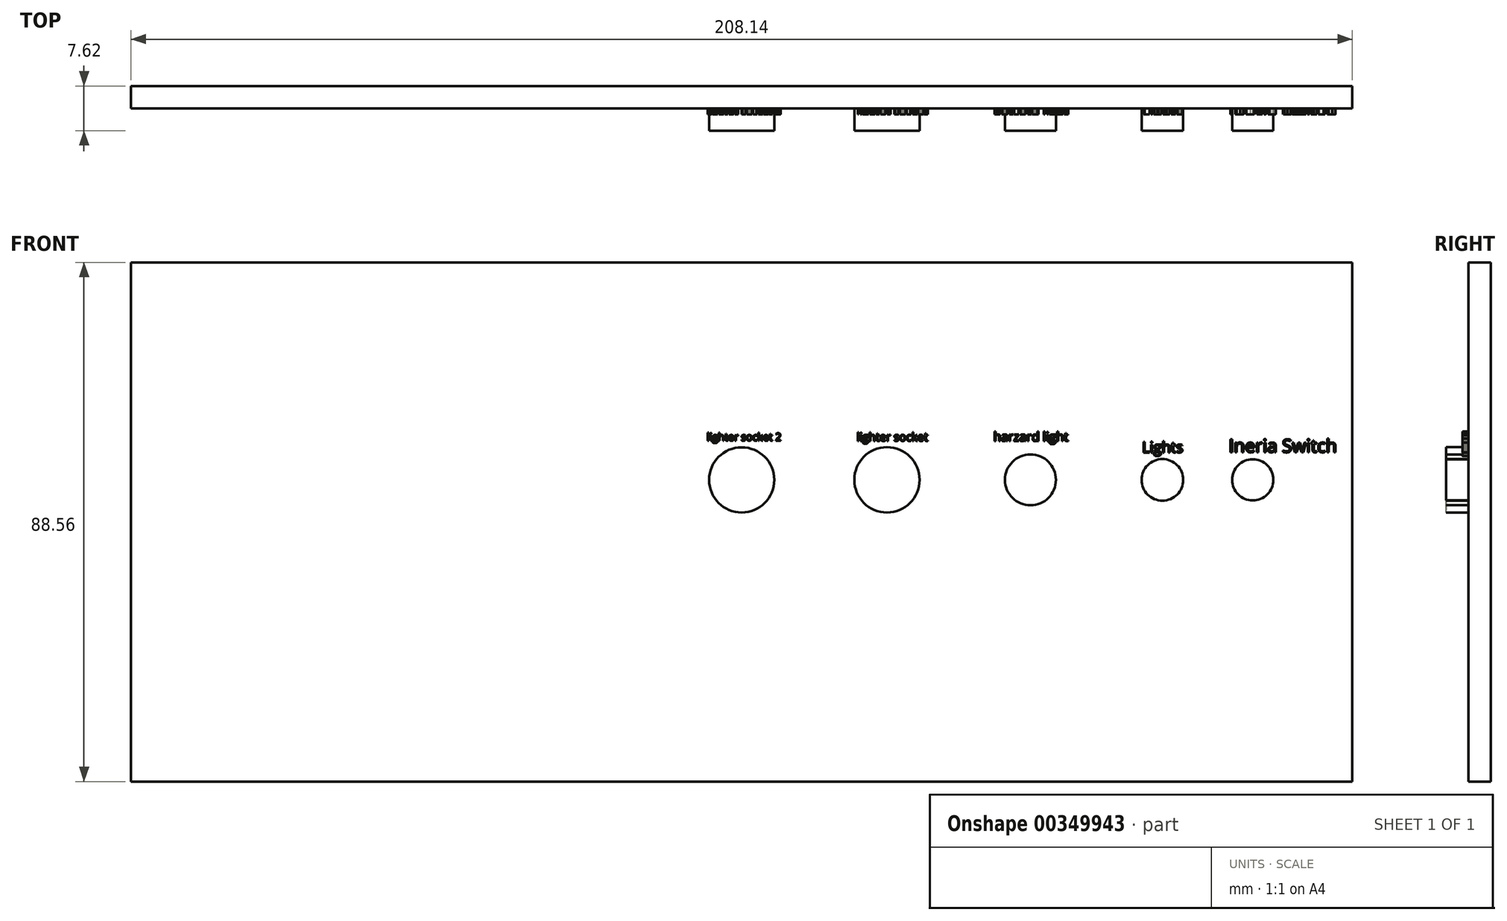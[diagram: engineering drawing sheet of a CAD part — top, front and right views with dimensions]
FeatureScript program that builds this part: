
annotation { "Feature Type Name" : "Feature", "Feature Type Description" : "" }
export const myFeature = defineFeature(function(context is Context, id is Id, definition is map)
    precondition{}
    {
        {
            var Q0;
            Q0=qCreatedBy(makeId("Front.planeOp"),FACE);
            var sketch = newSketch(context, id + "F0", { "sketchPlane" : qUnion([Q0])});
            skLineSegment(sketch, "E0.bottom", {"start": v(104.07, -44.28) * mm, "end": v(-104.07, -44.28) * mm});
            skLineSegment(sketch, "E0.top", {"start": v(104.07, 44.28) * mm, "end": v(-104.07, 44.28) * mm});
            skLineSegment(sketch, "E0.left", {"start": v(104.07, -44.28) * mm, "end": v(104.07, 44.28) * mm});
            skLineSegment(sketch, "E0.right", {"start": v(-104.07, -44.28) * mm, "end": v(-104.07, 44.28) * mm});
            skPoint(sketch, "E0.middle", {"position": v(0, 0) * mm});
            skSolve(sketch);
        }
        {
            var Q0;
            Q0 = qSketchRegion(id + "F0", true);
            extrude(context, id + "F1", {"entities" : qUnion([Q0]), "depth" : 3.8 * mm, "offsetDistance" : 25.4 * mm});
        }
        {
            var Q0;
            Q0=makeQuery(id+"F1.opExtrude","CAP_FACE",FACE,{"disambiguationData":[OSD([sQuery(id+"F0.wireOp",EDGE,"E0.bottom"),sQuery(id+"F0.wireOp",EDGE,"E0.top"),sQuery(id+"F0.wireOp",EDGE,"E0.left"),sQuery(id+"F0.wireOp",EDGE,"E0.right")])],"isStart":false});
            var sketch = newSketch(context, id + "F2", { "sketchPlane" : qUnion([Q0])});
            skCircle(sketch, "E1", {"center": v(71.7, 7.19) * mm, "radius": 3.55 * mm});
            skCircle(sketch, "E2", {"center": v(49.22, 7.19) * mm, "radius": 4.34 * mm});
            skCircle(sketch, "E3", {"center": v(24.76, 7.19) * mm, "radius": 5.56 * mm});
            skCircle(sketch, "E4", {"center": v(0, 7.19) * mm, "radius": 5.55 * mm});
            skCircle(sketch, "E5", {"center": v(87.1, 7.19) * mm, "radius": 3.51 * mm});
            skSolve(sketch);
        }
        {
            var Q0;
            Q0 = qSketchRegion(id + "F2", true);
            extrude(context, id + "F3", {"entities" : qUnion([Q0]), "operationType" : NewBodyOperationType.ADD, "depth" : 3.8 * mm, "offsetDistance" : 25.4 * mm});
        }
        {
            var Q0;
            {var subQ0=sQuery(id+"F0.wireOp",EDGE,"E0.right");var subQ1=sQuery(id+"F0.wireOp",EDGE,"E0.left");var subQ2=sQuery(id+"F0.wireOp",EDGE,"E0.bottom");var subQ3=sQuery(id+"F0.wireOp",EDGE,"E0.top");Q0=makeQuery(id+"FKdQGaDc0laFqGK_1.boolean.opBoolean","SPLIT",FACE,{"disambiguationData":[TD([makeQuery(id+"F1.opExtrude","SWEPT_FACE",FACE,{"disambiguationData":[OSD([subQ2])]})])],"derivedFrom":makeQuery(id+"F1.opExtrude","CAP_FACE",FACE,{"disambiguationData":[OSD([subQ2,subQ3,subQ1,subQ0])],"isStart":false})});}
            var sketch = newSketch(context, id + "F4", { "sketchPlane" : qUnion([Q0])});
            skText(sketch, "E6", { "text": "harzard light\n", "fontName": "OpenSans-Regular.ttf"});
            skText(sketch, "E7", { "text": " lighter socket ", "fontName": "OpenSans-Regular.ttf"});
            skText(sketch, "E8", { "text": "lighter socket 2", "fontName": "OpenSans-Regular.ttf"});
            skText(sketch, "E9", { "text": "Lights\n", "fontName": "OpenSans-Regular.ttf"});
            skText(sketch, "E10", { "text": "Ineria Switch\n", "fontName": "OpenSans-Regular.ttf"});
            const initialGuessF4  = {"E6": [0.0429, 0.01379, 1, 0, 0.00156], "E7": [0.0191, 0.01382, 1, 0, 0.0014], "E8": [-0.00592, 0.01388, 1, 0, 0.00129], "E9": [0.06823, 0.01186, 1, 0, 0.00183], "E10": [0.08302, 0.01189, 1, 0, 0.00223]};
            skSetInitialGuess(sketch, initialGuessF4);
            skSolve(sketch);
        }
        {
            var Q0;
            Q0 = qSketchRegion(id + "F4", true);
            extrude(context, id + "F5", {"entities" : qUnion([Q0]), "operationType" : NewBodyOperationType.ADD, "depth" : 1.02 * mm, "offsetDistance" : 25.4 * mm});
        }
    });
